# Revit family: revitupgrade
name_source: partatom
category: Furniture
units: mm (PartAtom-declared; Revit-internal decimal feet)

## family parameters
Always vertical = Yes
Cut with Voids When Loaded = No
Enable Cutting in Views = No
OmniClass Number = 23.40.70.14.64.11
OmniClass Title = Office Furniture
Render Appearance Source = Family Geometry
Room Calculation Point = No
Shared = No
Work Plane-Based = No

## types (2) — shared parameters
Arms Finish = Steelcase - 6400 Black
Assembly Code = E2020200
Description = Personality™ Plus incorporating Steelcase's Seating Insights and the industry's highest quality standards, the goal of our re-design efforts was to elevate the everyday comfort, performance and experience of people at work.
Frame = Steelcase - 6400 Black
Manufacturer = Steelcase
Release Date = October 2024
URL = https://www.steelcase.com
zero-valued in all types: Default Elevation

## per-type parameters (varying)
| type | Mesh Back | Style Number(s) |
| Mesh Back | Yes | PUA100,PUA100CN |
| Upholstery Back | No | PUA200,PUA200CN |

type visibility flags (boolean, named after types; folded from table):
- Mesh Back: Yes: (none)
- Upholstery Back: Yes: Upholstery Back

## geometry (parser evidence)
native form markers: Sweep x5
no freeform markers — native parametric forms only
